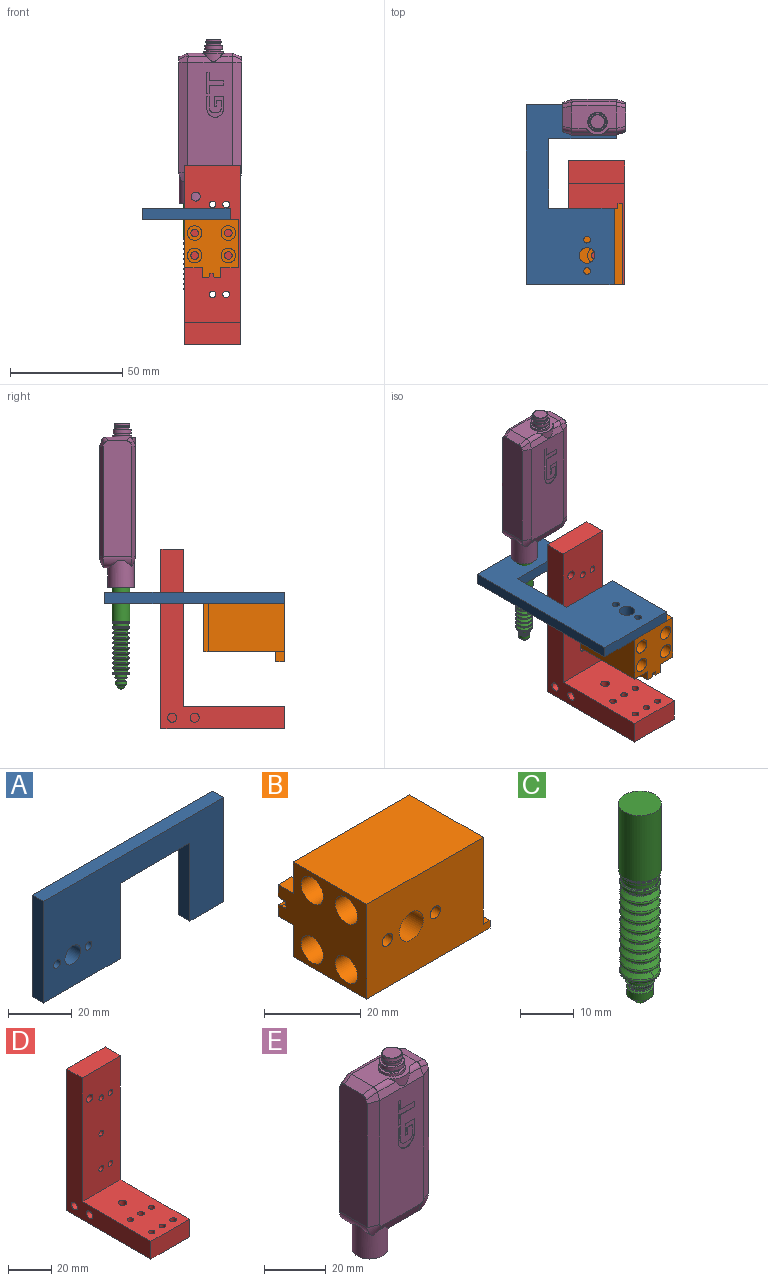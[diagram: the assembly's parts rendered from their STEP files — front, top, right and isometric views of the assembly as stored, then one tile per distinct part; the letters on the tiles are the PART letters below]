
ASSEMBLY  parts=5 mates=6
PART A: 13 faces, bbox 80x5x40 mm
  f0: plane 80x40mm, normal (0,-1,0), area 2183.4mm2, adj f1,f3,f4,f5,f6,f7,f8,f9
  f1: plane 39x5mm, normal (-1,0,0), area 195mm2, adj f0,f2,f3,f12
  f2: plane 80x40mm, normal (0,1,0), area 2183.4mm2, adj f1,f3,f4,f5,f6,f7,f8,f9
  f3: plane 34x5mm, normal (0,0,-1), area 170mm2, adj f0,f1,f2,f6
  f4: cylinder r=1.5mm len=5mm, axis (0,-1,0), area 47.1mm2, adj f0,f2
  f5: cylinder r=1.5mm len=5mm, axis (0,-1,0), area 47.1mm2, adj f0,f2
  f6: plane 29x5mm, normal (1,0,0), area 145mm2, adj f0,f2,f3,f8
  f7: cylinder r=3.5mm len=7mm, axis (0,-1,0), area 110mm2, adj f0,f2
  f8: plane 31x5mm, normal (0,0,-1), area 155mm2, adj f0,f2,f6,f10
  f9: plane 40x5mm, normal (1,0,0), area 200mm2, adj f0,f2,f11,f12
  f10: plane 30x5mm, normal (-1,0,0), area 150mm2, adj f0,f2,f8,f11
  f11: plane 15x5mm, normal (0,0,-1), area 75mm2, adj f0,f2,f9,f10
  f12: plane 80x5mm, normal (0,0,1), area 400mm2, adj f0,f1,f2,f9
PART B: 41 faces, bbox 36x26x24 mm
  f0: cylinder r=1.75mm len=6.5mm, axis (0,-1,0), area 71.5mm2, adj f2,f35
  f1: plane 21.5x2mm, normal (1,0,0), area 43mm2, adj f2,f3,f10,f33
  f2: plane 36x24mm, normal (0,1,0), area 771.3mm2, adj f0,f1,f8,f9,f10,f11,f12,f20
  f3: plane 36x24mm, normal (0,-1,0), area 767.4mm2, adj f1,f8,f9,f10,f29,f31,f33,f34
  f4: cylinder r=1.7mm len=27.5mm, axis (-1,0,0), area 293.7mm2, adj f27,f34
  f5: cylinder r=1.7mm len=27.5mm, axis (-1,0,0), area 293.7mm2, adj f25,f34
  f6: cylinder r=1.7mm len=27.5mm, axis (-1,0,0), area 293.7mm2, adj f23,f34
  f7: cylinder r=1.7mm len=27.5mm, axis (-1,0,0), area 293.7mm2, adj f21,f34
  f8: plane 34x21.5mm, normal (0,0,1), area 731mm2, adj f2,f3,f9,f34
  f9: plane 26x24mm, normal (-1,0,0), area 415.2mm2, adj f2,f3,f8,f10,f11,f12,f13,f14
  f10: plane 36x21.5mm, normal (0,0,-1), area 766.9mm2, adj f1,f2,f3,f9,f37
  f11: plane 4.5x4mm, normal (0,0,-1), area 18mm2, adj f2,f9,f19,f20
  f12: plane 4.5x4mm, normal (0,0,1), area 18mm2, adj f2,f9,f13,f20
  f13: plane 4x2.87mm, normal (0,1,0), area 11.5mm2, adj f9,f12,f14,f20
  f14: plane 4x1mm, normal (0,0.26,-0.97), area 4.1mm2, adj f9,f13,f15,f20
  f15: plane 4x1.2mm, normal (0,0,-1), area 4.8mm2, adj f9,f14,f16,f20
  f16: plane 4x1.72mm, normal (0,1,0), area 6.9mm2, adj f9,f15,f17,f20
  f17: plane 4x1.2mm, normal (0,0,1), area 4.8mm2, adj f9,f16,f18,f20
  f18: plane 4x1mm, normal (0,0.26,0.97), area 4.1mm2, adj f9,f17,f19,f20
  f19: plane 4x2.87mm, normal (0,1,0), area 11.5mm2, adj f9,f11,f18,f20
  f20: plane 8x4.5mm, normal (1,0,0), area 31.9mm2, adj f2,f11,f12,f13,f14,f15,f16,f17
  f21: plane 6.5x6.5mm, normal (-1,0,0), area 24.1mm2, adj f7,f22
  f22: cylinder r=3.25mm len=6.5mm, axis (-1,0,0), area 132.7mm2, adj f9,f21
  f23: plane 6.5x6.5mm, normal (-1,0,0), area 24.1mm2, adj f6,f24
  f24: cylinder r=3.25mm len=6.5mm, axis (-1,0,0), area 132.7mm2, adj f9,f23
  f25: plane 6.5x6.5mm, normal (-1,0,0), area 24.1mm2, adj f5,f26
  f26: cylinder r=3.25mm len=6.5mm, axis (-1,0,0), area 132.7mm2, adj f9,f25
  f27: plane 6.5x6.5mm, normal (-1,0,0), area 24.1mm2, adj f4,f28
  f28: cylinder r=3.25mm len=6.5mm, axis (-1,0,0), area 132.7mm2, adj f9,f27
  f29: cylinder r=1.5mm len=6mm, axis (0,-1,0), area 56.5mm2, adj f3,f30
  f30: plane 3x3mm, normal (0,-1,0), area 7.1mm2, adj f29
  f31: cylinder r=1.5mm len=6mm, axis (0,-1,0), area 56.5mm2, adj f3,f32
  f32: plane 3x3mm, normal (0,-1,0), area 7.1mm2, adj f31
  f33: plane 21.5x2mm, normal (0,0,1), area 43mm2, adj f1,f2,f3,f34
  f34: plane 22x21.5mm, normal (1,0,0), area 436.7mm2, adj f2,f3,f4,f5,f6,f7,f8,f33
  f35: plane 7x7mm, normal (0,-1,0), area 28.9mm2, adj f0,f36
  f36: cylinder r=3.5mm len=15mm, axis (0,-1,0), area 329.9mm2, adj f3,f35
  f37: cylinder r=1.5mm len=6mm, axis (0,0,-1), area 56.5mm2, adj f10,f38
  f38: plane 3x3mm, normal (0,0,-1), area 7.1mm2, adj f37
  f39: cylinder r=1.5mm len=6mm, axis (0,1,0), area 56.5mm2, adj f2,f40
  f40: plane 3x3mm, normal (0,1,0), area 7.1mm2, adj f39
PART C: 72 faces, bbox 8.2x8.2x45.3 mm
  f0: sphere r=1.5mm, area 10.4mm2, adj f1
  f1: plane 3.4x3.4mm, normal (0,0,-1), area 2.5mm2, adj f0,f2,f3
  f2: cone r=2.5mm half-angle=45deg, axis (0,0,1), area 7.5mm2, adj f1,f3,f4
  f3: cone r=2.5mm half-angle=45deg, axis (0,0,1), area 7.5mm2, adj f1,f2,f4
  f4: cylinder r=2.5mm len=5mm, axis (0,0,-1), area 25.1mm2, adj f2,f3,f5,f6
  f5: cone r=2.5mm half-angle=45deg, axis (0,0,-1), area 3.1mm2, adj f4,f6,f7
  f6: cone r=2.5mm half-angle=45deg, axis (0,0,-1), area 3.1mm2, adj f4,f5,f7
  f7: plane 4.4x4.4mm, normal (0,0,1), area 5mm2, adj f5,f6,f8
  f8: torus R=1.8mm, axis (0,0,-1), area 3.8mm2, adj f7,f9
  f9: cylinder r=2mm len=4mm, axis (0,0,-1), area 9.4mm2, adj f8,f10
  f10: plane 5.2x5.2mm, normal (0,0,-1), area 8.7mm2, adj f9,f11
  f11: cone r=2.8mm half-angle=26.6deg, axis (0,0,1), area 7.6mm2, adj f10,f12
  f12: cylinder r=2.8mm len=5.6mm, axis (0,0,-1), area 1.8mm2, adj f11,f13
  f13: plane 5.6x5.6mm, normal (0,0,1), area 5mm2, adj f12,f14
  f14: cylinder r=2.5mm len=5mm, axis (0,0,-1), area 17.3mm2, adj f13,f15
  f15: torus R=2.7mm, axis (0,0,-1), area 5.1mm2, adj f14,f16
  f16: plane 6.4x6.4mm, normal (0,0,-1), area 9.3mm2, adj f15,f17
  f17: torus R=3.2mm, axis (0,0,-1), area 21.2mm2, adj f16,f18
  f18: cylinder r=3.8mm len=7.6mm, axis (0,0,-1), area 2.4mm2, adj f17,f19
  f19: torus R=3.4mm, axis (0,0,-1), area 7.9mm2, adj f18,f20,f21
  f20: cone r=3.67mm half-angle=48.2deg, axis (0,0,-1), area 11.5mm2, adj f19,f21,f22
  f21: cone r=3.67mm half-angle=48.2deg, axis (0,0,-1), area 11.5mm2, adj f19,f20,f22
  f22: torus R=2.88mm, axis (0,0,-1), area 2.4mm2, adj f20,f21,f23
  f23: cone r=3.67mm half-angle=48.2deg, axis (0,0,1), area 23mm2, adj f22,f24
  f24: torus R=3.4mm, axis (0,0,-1), area 15.9mm2, adj f23,f25
  f25: cone r=3.67mm half-angle=48.2deg, axis (0,0,-1), area 23mm2, adj f24,f26
  f26: torus R=2.88mm, axis (0,0,-1), area 2.4mm2, adj f25,f27
  f27: cone r=3.67mm half-angle=48.2deg, axis (0,0,1), area 23mm2, adj f26,f28
  f28: torus R=3.4mm, axis (0,0,-1), area 15.9mm2, adj f27,f29
  f29: cone r=3.67mm half-angle=48.2deg, axis (0,0,-1), area 23mm2, adj f28,f30
  f30: torus R=2.88mm, axis (0,0,-1), area 2.4mm2, adj f29,f31
  f31: cone r=3.67mm half-angle=48.2deg, axis (0,0,1), area 23mm2, adj f30,f32
  f32: torus R=3.4mm, axis (0,0,-1), area 15.9mm2, adj f31,f33
  f33: cone r=3.67mm half-angle=48.2deg, axis (0,0,-1), area 23mm2, adj f32,f34
  f34: torus R=2.88mm, axis (0,0,-1), area 2.4mm2, adj f33,f35
  f35: cone r=3.67mm half-angle=48.2deg, axis (0,0,1), area 23mm2, adj f34,f36
  f36: torus R=3.4mm, axis (0,0,-1), area 15.9mm2, adj f35,f37
  f37: cone r=3.67mm half-angle=48.2deg, axis (0,0,-1), area 23mm2, adj f36,f38
  f38: torus R=2.88mm, axis (0,0,-1), area 2.4mm2, adj f37,f39
  f39: cone r=3.67mm half-angle=48.2deg, axis (0,0,1), area 23mm2, adj f38,f40
  f40: torus R=3.4mm, axis (0,0,-1), area 15.9mm2, adj f39,f41
  f41: cone r=3.67mm half-angle=48.2deg, axis (0,0,-1), area 23mm2, adj f40,f42
  f42: torus R=2.88mm, axis (0,0,-1), area 2.4mm2, adj f41,f43,f44
  f43: cone r=3.67mm half-angle=48.2deg, axis (0,0,1), area 11.5mm2, adj f42,f44,f45
  f44: cone r=3.67mm half-angle=48.2deg, axis (0,0,1), area 11.5mm2, adj f42,f43,f45
  f45: torus R=3.4mm, axis (0,0,-1), area 15.9mm2, adj f43,f44,f46
  f46: cone r=3.67mm half-angle=48.2deg, axis (0,0,-1), area 23mm2, adj f45,f47
  f47: torus R=2.88mm, axis (0,0,-1), area 2.4mm2, adj f46,f48
  f48: cone r=3.67mm half-angle=48.2deg, axis (0,0,1), area 23mm2, adj f47,f49
  f49: torus R=3.4mm, axis (0,0,-1), area 15.9mm2, adj f48,f50
  f50: cone r=3.67mm half-angle=48.2deg, axis (0,0,-1), area 23mm2, adj f49,f51
  f51: torus R=2.88mm, axis (0,0,-1), area 2.4mm2, adj f50,f52,f53
  f52: cone r=3.67mm half-angle=48.2deg, axis (0,0,1), area 11.5mm2, adj f51,f53,f54
  f53: cone r=3.67mm half-angle=48.2deg, axis (0,0,1), area 11.5mm2, adj f51,f52,f54
  f54: torus R=3.4mm, axis (0,0,-1), area 15.9mm2, adj f52,f53,f55
  f55: cone r=3.67mm half-angle=48.2deg, axis (0,0,-1), area 23mm2, adj f54,f56
  f56: torus R=2.88mm, axis (0,0,-1), area 2.4mm2, adj f55,f57
  f57: cone r=3.67mm half-angle=48.2deg, axis (0,0,1), area 23mm2, adj f56,f58
  f58: torus R=3.4mm, axis (0,0,-1), area 7.9mm2, adj f57,f59
  f59: cylinder r=3.8mm len=7.6mm, axis (0,0,-1), area 11.9mm2, adj f58,f60
  f60: torus R=3.6mm, axis (0,0,-1), area 7.3mm2, adj f59,f61
  f61: plane 7.2x7.2mm, normal (0,0,1), area 1.1mm2, adj f60,f62
  f62: torus R=3.55mm, axis (0,0,-1), area 5.1mm2, adj f61,f63
  f63: cylinder r=3.4mm len=6.8mm, axis (0,0,-1), area 24.6mm2, adj f62,f64
  f64: plane 7.6x7.6mm, normal (0,0,-1), area 9mm2, adj f63,f65
  f65: cylinder r=3.8mm len=7.6mm, axis (0,0,-1), area 11.9mm2, adj f64,f66
  f66: plane 7.6x7.6mm, normal (0,0,1), area 4.6mm2, adj f65,f67
  f67: cone r=3.8mm half-angle=45deg, axis (0,0,1), area 6.6mm2, adj f66,f68
  f68: cylinder r=3.8mm len=7.6mm, axis (0,0,-1), area 7.2mm2, adj f67,f70
  f69: plane 8x8mm, normal (0,0,1), area 50.3mm2, adj f71
  f70: plane 8x8mm, normal (0,0,-1), area 4.9mm2, adj f68,f71
  f71: cylinder r=4mm len=15.1mm, axis (0,0,-1), area 379.5mm2, adj f69,f70
PART D: 27 faces, bbox 25x55x80 mm
  f0: plane 70x25mm, normal (0,-1,0), area 1702.1mm2, adj f1,f3,f4,f6,f8,f9,f10,f11
  f1: plane 80x55mm, normal (-1,0,0), area 1224.9mm2, adj f0,f2,f4,f5,f6,f7,f23,f25
  f2: plane 55x25mm, normal (0,0,-1), area 1320mm2, adj f1,f3,f5,f7,f16,f17,f18,f19
  f3: plane 80x55mm, normal (1,0,0), area 1242.9mm2, adj f0,f2,f4,f5,f6,f7,f14
  f4: plane 25x10mm, normal (0,0,1), area 250mm2, adj f0,f1,f3,f5
  f5: plane 80x25mm, normal (0,1,0), area 1952.1mm2, adj f1,f2,f3,f4,f8,f9,f10,f11
  f6: plane 45x25mm, normal (0,0,1), area 1070mm2, adj f0,f1,f3,f7,f16,f17,f18,f19
  f7: plane 25x10mm, normal (0,-1,0), area 250mm2, adj f1,f2,f3,f6
  f8: cylinder r=1.5mm len=10mm, axis (0,-1,0), area 94.2mm2, adj f0,f5
  f9: cylinder r=1.5mm len=10mm, axis (0,-1,0), area 94.2mm2, adj f0,f5
  f10: cylinder r=1.5mm len=10mm, axis (0,-1,0), area 94.2mm2, adj f0,f5
  f11: cylinder r=1.5mm len=10mm, axis (0,-1,0), area 94.2mm2, adj f0,f5
  f12: cylinder r=1.5mm len=10mm, axis (0,-1,0), area 94.2mm2, adj f0,f5
  f13: cylinder r=2mm len=10mm, axis (0,-1,0), area 125.7mm2, adj f0,f5
  f14: cylinder r=1.5mm len=6mm, axis (1,0,0), area 56.5mm2, adj f3,f15
  f15: plane 3x3mm, normal (1,0,0), area 7.1mm2, adj f14
  f16: cylinder r=1.5mm len=10mm, axis (0,0,1), area 94.2mm2, adj f2,f6
  f17: cylinder r=1.5mm len=10mm, axis (0,0,1), area 94.2mm2, adj f2,f6
  f18: cylinder r=1.5mm len=10mm, axis (0,0,1), area 94.2mm2, adj f2,f6
  f19: cylinder r=2mm len=10mm, axis (0,0,1), area 125.7mm2, adj f2,f6
  f20: cylinder r=1.5mm len=10mm, axis (0,0,1), area 94.2mm2, adj f2,f6
  f21: cylinder r=1.5mm len=10mm, axis (0,0,1), area 94.2mm2, adj f2,f6
  f22: cylinder r=1.5mm len=10mm, axis (0,0,1), area 94.2mm2, adj f2,f6
  f23: cylinder r=2mm len=10mm, axis (-1,0,0), area 125.7mm2, adj f1,f24
  f24: plane 4x4mm, normal (-1,0,0), area 12.6mm2, adj f23
  f25: cylinder r=2mm len=10mm, axis (-1,0,0), area 125.7mm2, adj f1,f26
  f26: plane 4x4mm, normal (-1,0,0), area 12.6mm2, adj f25
PART E: 77 faces, bbox 28.6x16.3x73.4 mm
  f0: plane 6.16x6.16mm, normal (0,0,1), area 29.8mm2, adj f1
  f1: torus R=3.08mm, axis (0,0,-1), area 5.7mm2, adj f0,f2
  f2: cone r=3.45mm half-angle=9.1deg, axis (0,0,-1), area 23.1mm2, adj f1,f3
  f3: cylinder r=3.45mm len=6.9mm, axis (0,0,-1), area 10.8mm2, adj f2,f4
  f4: cone r=3.45mm half-angle=38.7deg, axis (0,0,1), area 6.7mm2, adj f3,f5
  f5: cylinder r=3.25mm len=6.5mm, axis (0,0,-1), area 20.4mm2, adj f4,f6
  f6: plane 8.12x8.12mm, normal (0,0,1), area 17.1mm2, adj f5,f7
  f7: cylinder r=4mm len=8mm, axis (0,0,-1), area 37.7mm2, adj f6,f8
  f8: plane 8.12x8.12mm, normal (0,0,-1), area 4.9mm2, adj f7,f9
  f9: cylinder r=3.8mm len=7.6mm, axis (0,0,-1), area 7.2mm2, adj f8,f10
  f10: plane 7.71x7.71mm, normal (0,0,-1), area 9.1mm2, adj f9,f11
  f11: cylinder r=3.4mm len=6.8mm, axis (0,0,-1), area 12.8mm2, adj f10,f14
  f12: plane 9.56x7.56mm, normal (0,-1,0), area 35mm2, adj f15,f16,f17,f18,f19,f20,f21,f22
  f13: plane 9.5x7.5mm, normal (0,-1,0), area 23.8mm2, adj f31,f32,f33,f34,f35,f36,f37,f38
  f14: plane 8.73x8.73mm, normal (0,0,1), area 21.8mm2, adj f11,f43
  f15: cylinder r=3.27mm len=3.16mm, axis (0,-1,0), area 0.8mm2, adj f12,f16,f30,f46
  f16: cylinder r=4.2mm len=3.68mm, axis (0,-1,0), area 1.1mm2, adj f12,f15,f17,f46
  f17: plane 5.42x0.25mm, normal (-1,0,0), area 1.4mm2, adj f12,f16,f18,f46
  f18: plane 4.25x0.25mm, normal (0,0,-1), area 1.1mm2, adj f12,f17,f19,f46
  f19: plane 4.5x0.25mm, normal (1,0,0), area 1.1mm2, adj f12,f18,f20,f46
  f20: plane 1x0.25mm, normal (0,0,1), area 0.2mm2, adj f12,f19,f21,f46
  f21: plane 2.5x0.25mm, normal (-1,0,0), area 0.6mm2, adj f12,f20,f22,f46
  f22: plane 2.25x0.25mm, normal (0,0,1), area 0.6mm2, adj f12,f21,f23,f46
  f23: plane 3.3x0.25mm, normal (1,0,0), area 0.8mm2, adj f12,f22,f24,f46
  f24: cylinder r=2mm len=2mm, axis (0,-1,0), area 0.8mm2, adj f12,f23,f25,f46
  f25: plane 1.5x0.25mm, normal (0,0,-1), area 0.4mm2, adj f12,f24,f26,f46
  f26: cylinder r=2mm len=2mm, axis (0,-1,0), area 0.8mm2, adj f12,f25,f27,f46
  f27: plane 5.3x0.25mm, normal (-1,0,0), area 1.3mm2, adj f12,f26,f28,f46
  f28: plane 1x0.25mm, normal (0,0,-1), area 0.3mm2, adj f12,f27,f29,f46
  f29: plane 5.42x0.25mm, normal (1,0,0), area 1.4mm2, adj f12,f28,f30,f46
  f30: cylinder r=4.2mm len=3.68mm, axis (0,-1,0), area 1.1mm2, adj f12,f15,f29,f46
  f31: plane 3.65x0.25mm, normal (-1,0,0), area 0.9mm2, adj f13,f32,f38,f46
  f32: plane 1x0.25mm, normal (0,0,-1), area 0.3mm2, adj f13,f31,f33,f46
  f33: plane 9.5x0.25mm, normal (1,0,0), area 2.4mm2, adj f13,f32,f34,f46
  f34: plane 1x0.25mm, normal (0,0,1), area 0.3mm2, adj f13,f33,f35,f46
  f35: plane 3.65x0.25mm, normal (-1,0,0), area 0.9mm2, adj f13,f34,f36,f46
  f36: plane 6.5x0.25mm, normal (0,0,1), area 1.6mm2, adj f13,f35,f37,f46
  f37: plane 2.2x0.25mm, normal (-1,0,0), area 0.5mm2, adj f13,f36,f38,f46
  f38: plane 6.5x0.25mm, normal (0,0,-1), area 1.6mm2, adj f13,f31,f37,f46
  f39: plane 20x2.74mm, normal (0,-0.93,0.37), area 47.5mm2, adj f40,f41,f42,f44,f45,f46
  f40: plane 4.22x2.94mm, normal (-0.34,-0.86,0.37), area 10mm2, adj f39,f41,f51,f53,f64
  f41: cylinder r=2mm len=8.34mm, axis (1,0,0), area 17.6mm2, adj f39,f40,f42,f52,f53,f55
  f42: cylinder r=5.75mm len=9.88mm, axis (0,0,-1), area 22.2mm2, adj f39,f41,f45,f55
  f43: cylinder r=4.3mm len=8.6mm, axis (0,0,-1), area 25.7mm2, adj f14,f55
  f44: plane 4.23x2.96mm, normal (0.34,-0.86,0.37), area 10mm2, adj f39,f45,f57,f58,f68
  f45: cylinder r=2mm len=5.34mm, axis (1,0,0), area 10.3mm2, adj f39,f42,f44,f55,f58
  f46: plane 50.11x20.06mm, normal (0,-1,0), area 941.7mm2, adj f15,f16,f17,f18,f19,f20,f21,f22
  f47: cone r=5mm half-angle=68.2deg, axis (0,1,0), area 20.3mm2, adj f46,f57,f60,f61
  f48: plane 11.6x11.6mm, normal (0,0,-1), area 105.7mm2, adj f62
  f49: plane 1.96x0.08mm, normal (0,0,1), area 0.1mm2, adj f62,f63
  f50: cone r=5mm half-angle=68.2deg, axis (0,1,0), area 17.9mm2, adj f46,f51,f60,f62,f63
  f51: plane 49.05x4mm, normal (-0.37,-0.93,0), area 211.3mm2, adj f40,f46,f50,f64
  f52: plane 10.11x4mm, normal (-0.37,0,0.93), area 39.6mm2, adj f41,f53,f54,f55,f64,f66
  f53: cylinder r=2mm len=4.34mm, axis (-0.91,0.21,-0.36), area 9.7mm2, adj f40,f41,f52,f64
  f54: cylinder r=2mm len=4.34mm, axis (-0.91,-0.21,-0.36), area 9.7mm2, adj f52,f64,f65,f66
  f55: plane 20.13x13.02mm, normal (0,0,1), area 163.3mm2, adj f41,f42,f43,f45,f52,f59,f66
  f56: cylinder r=2mm len=4.34mm, axis (-0.91,0.21,0.36), area 9.7mm2, adj f59,f66,f67,f68
  f57: plane 49.05x4mm, normal (0.37,-0.93,0), area 211.3mm2, adj f44,f46,f47,f68
  f58: cylinder r=2mm len=4.34mm, axis (-0.91,-0.21,0.36), area 9.7mm2, adj f44,f45,f59,f68
  f59: plane 10.1x4mm, normal (0.37,0,0.93), area 39.6mm2, adj f55,f56,f58,f66,f68
  f60: plane 18x4mm, normal (0,-0.93,-0.37), area 69mm2, adj f46,f47,f50,f62,f70
  f61: cylinder r=5mm len=12.8mm, axis (0,1,0), area 100.5mm2, adj f47,f68,f69,f70
  f62: cylinder r=5.8mm len=12.04mm, axis (0,0,1), area 353.5mm2, adj f48,f49,f50,f60,f63,f70
  f63: cylinder r=5mm len=12.8mm, axis (0,1,0), area 57.6mm2, adj f49,f50,f62,f64,f70,f71
  f64: plane 51.71x13.06mm, normal (-1,0,0), area 655.6mm2, adj f40,f51,f52,f53,f54,f63,f65,f72
  f65: plane 4.21x2.94mm, normal (-0.34,0.86,0.37), area 10mm2, adj f54,f64,f66,f72,f73
  f66: cylinder r=2mm len=20mm, axis (-1,0,0), area 47.3mm2, adj f52,f54,f55,f56,f59,f65,f67,f73
  f67: plane 4.21x2.94mm, normal (0.34,0.86,0.37), area 10mm2, adj f56,f66,f68,f73,f74
  f68: plane 51.71x13.06mm, normal (1,0,0), area 655.6mm2, adj f44,f56,f57,f58,f59,f61,f67,f74
  f69: cone r=5mm half-angle=68.2deg, axis (0,-1,0), area 20.3mm2, adj f61,f74,f75,f76
  f70: plane 18x12.8mm, normal (0,0,-1), area 169.2mm2, adj f60,f61,f62,f63,f75
  f71: cone r=5mm half-angle=68.2deg, axis (0,-1,0), area 20.3mm2, adj f63,f72,f75,f76
  f72: plane 49.05x4mm, normal (-0.37,0.93,0), area 211.3mm2, adj f64,f65,f71,f76
  f73: plane 20x2.74mm, normal (0,0.93,0.37), area 58.5mm2, adj f65,f66,f67,f76
  f74: plane 49.05x4mm, normal (0.37,0.93,0), area 211.3mm2, adj f67,f68,f69,f76
  f75: plane 18x4mm, normal (0,0.93,-0.37), area 77.5mm2, adj f69,f70,f71,f76
  f76: plane 50.05x20mm, normal (0,1,0), area 1000.6mm2, adj f69,f71,f72,f73,f74,f75
PLACE A rot(axis=(-0.58,-0.58,0.58),120deg) t=(6,44.32,-25.65)mm
PLACE B rot(axis=(-0.58,-0.58,0.58),120deg) t=(9.74,44.32,-30.65)mm
PLACE C t=(1.15,99.11,-47.23)mm
PLACE D rot(axis=(-0.02,0,-1),0deg) t=(10.24,81.32,-24.95)mm
PLACE E t=(1.15,99.11,-47.23)mm
MATE parallel B.f8 <-> D.f1  axis (-1,0,0) through (-2.26,43.32,-19.9)mm
MATE parallel A.f5 <-> B.f31  axis (0,0,-1) through (6,32.32,-9.15)mm
MATE parallel E.f62 <-> C.f4  axis (0,0,-1) through (1.15,99.11,-1.93)mm
MATE parallel B.f2 <-> D.f6  axis (0,0,-1) through (9.79,43.97,-30.65)mm
MATE parallel A.f4 <-> B.f3  axis (0,0,-1) through (6,46.32,-9.15)mm
MATE parallel D.f7 <-> B.f9  axis (0,-1,0) through (10.24,26.32,-59.95)mm
